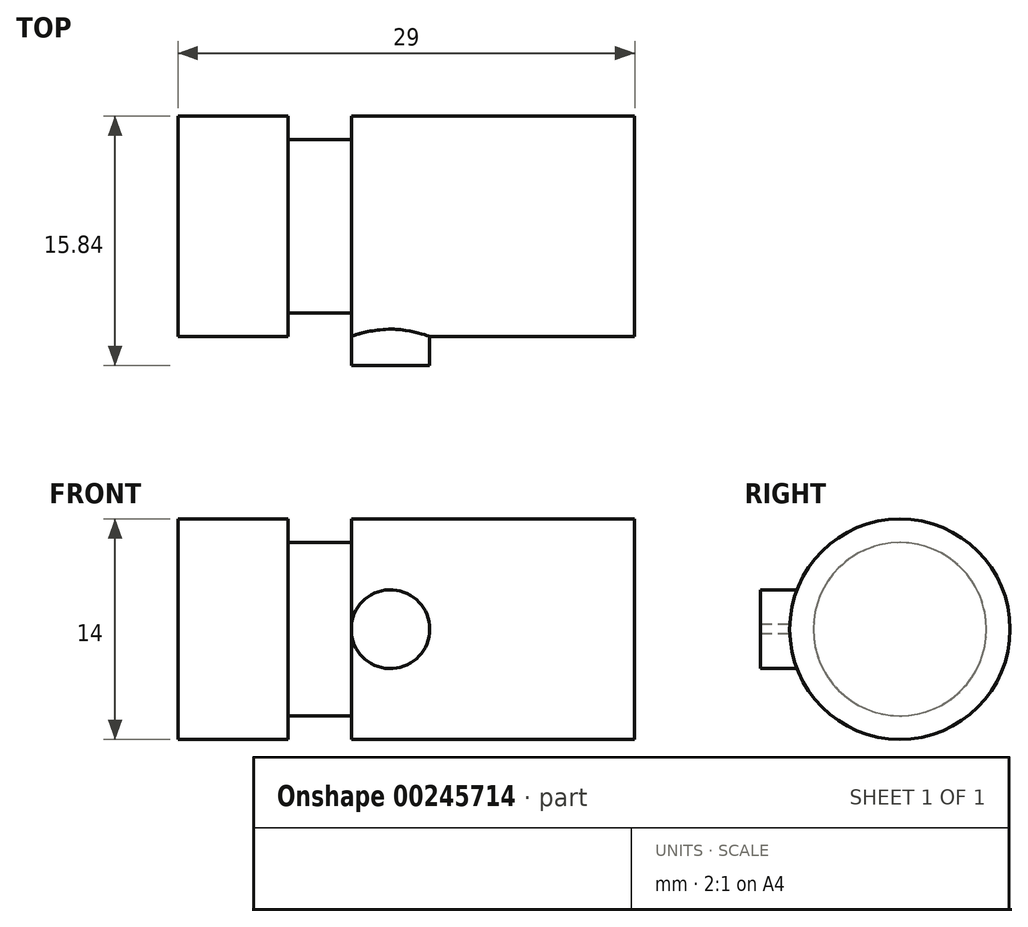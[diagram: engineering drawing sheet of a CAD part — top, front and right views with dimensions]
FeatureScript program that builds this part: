
annotation { "Feature Type Name" : "Feature", "Feature Type Description" : "" }
export const myFeature = defineFeature(function(context is Context, id is Id, definition is map)
    precondition{}
    {
        {
            var Q0;
            Q0=qCreatedBy(makeId("Front.planeOp"),FACE);
            var sketch = newSketch(context, id + "F0", { "sketchPlane" : qUnion([Q0])});
            skCircle(sketch, "E0", {"center": v(0, 0) * mm, "radius": 2.5 * mm});
            skSolve(sketch);
        }
        {
            var Q0;
            Q0=makeQuery(id+"F0.imprint","IMPRINT",FACE,{"disambiguationData":[TD([[makeQuery(id+"F0.imprint","IMPRINT",EDGE,{"derivedFrom":sQuery(id+"F0.wireOp",EDGE,"E0")}),1.0]])]});
            extrude(context, id + "F1", {"entities" : qUnion([Q0]), "depth" : 5 * mm});
        }
        {
            var Q0;
            Q0=makeQuery(id+"F1.opExtrude","CAP_FACE",FACE,{"disambiguationData":[OSD([sQuery(id+"F0.wireOp",EDGE,"E0")])],"isStart":false});
            var sketch = newSketch(context, id + "F2", { "sketchPlane" : qUnion([Q0])});
            skLineSegment(sketch, "E1.bottom", {"start": v(-2.48, -0.3) * mm, "end": v(-2.62, -0.3) * mm});
            skLineSegment(sketch, "E1.top", {"start": v(-2.48, 0.3) * mm, "end": v(-2.62, 0.3) * mm});
            skLineSegment(sketch, "E1.left", {"start": v(-2.48, -0.3) * mm, "end": v(-2.48, 0.3) * mm});
            skLineSegment(sketch, "E1.right", {"start": v(-2.62, -0.3) * mm, "end": v(-2.62, 0.3) * mm});
            skPoint(sketch, "E2", {"position": v(0, 0) * mm});
            skLineSegment(sketch, "E3", {"start": v(0, 0) * mm, "end": v(-4.13, 0) * mm, "construction": true});
            skSolve(sketch);
        }
        {
            var Q0;
            Q0 = qSketchRegion(id + "F2", true);
            extrude(context, id + "F3", {"entities" : qUnion([Q0]), "operationType" : NewBodyOperationType.REMOVE, "oppositeDirection" : true, "depth" : 25 * mm});
        }
        {
            var Q0;
            Q0=makeQuery(id+"F3.boolean.opBoolean","COPY",FACE,{"derivedFrom":makeQuery(id+"F3.opExtrude","SWEPT_FACE",FACE,{"disambiguationData":[OSD([sQuery(id+"F2.wireOp",EDGE,"E1.left")])]})});
            var sketch = newSketch(context, id + "F4", { "sketchPlane" : qUnion([Q0])});
            skCircle(sketch, "E4", {"center": v(-3.84, 0) * mm, "radius": 7 * mm});
            skSolve(sketch);
        }
        {
            var Q0;
            Q0 = qSketchRegion(id + "F4", true);
            extrude(context, id + "F5", {"entities" : qUnion([Q0]), "operationType" : NewBodyOperationType.ADD, "oppositeDirection" : true, "depth" : 18 * mm});
        }
        {
            var Q0;
            Q0=makeQuery(id+"F5.boolean.opBoolean","MERGE",FACE,{"derivedFrom":[makeQuery(id+"F3.boolean.opBoolean","COPY",FACE,{"derivedFrom":makeQuery(id+"F3.opExtrude","SWEPT_FACE",FACE,{"disambiguationData":[OSD([sQuery(id+"F2.wireOp",EDGE,"E1.left")])]})}),makeQuery(id+"F5.opExtrude","CAP_FACE",FACE,{"disambiguationData":[OSD([sQuery(id+"F4.wireOp",EDGE,"E4")])],"isStart":true})]});
            var sketch = newSketch(context, id + "F6", { "sketchPlane" : qUnion([Q0])});
            skCircle(sketch, "E5", {"center": v(-3.84, 0) * mm, "radius": 5.5 * mm});
            skSolve(sketch);
        }
        {
            var Q0;
            Q0 = qSketchRegion(id + "F6", true);
            extrude(context, id + "F7", {"entities" : qUnion([Q0]), "operationType" : NewBodyOperationType.ADD, "depth" : 4 * mm});
        }
        {
            var Q0;
            Q0=makeQuery(id+"F7.opExtrude","CAP_FACE",FACE,{"disambiguationData":[OSD([sQuery(id+"F6.wireOp",EDGE,"E5")])],"isStart":false});
            var sketch = newSketch(context, id + "F8", { "sketchPlane" : qUnion([Q0])});
            skCircle(sketch, "E6", {"center": v(-3.84, 0) * mm, "radius": 7 * mm});
            skSolve(sketch);
        }
        {
            var Q0;
            Q0 = qSketchRegion(id + "F8", true);
            extrude(context, id + "F9", {"entities" : qUnion([Q0]), "operationType" : NewBodyOperationType.ADD, "depth" : 7 * mm});
        }
    });
